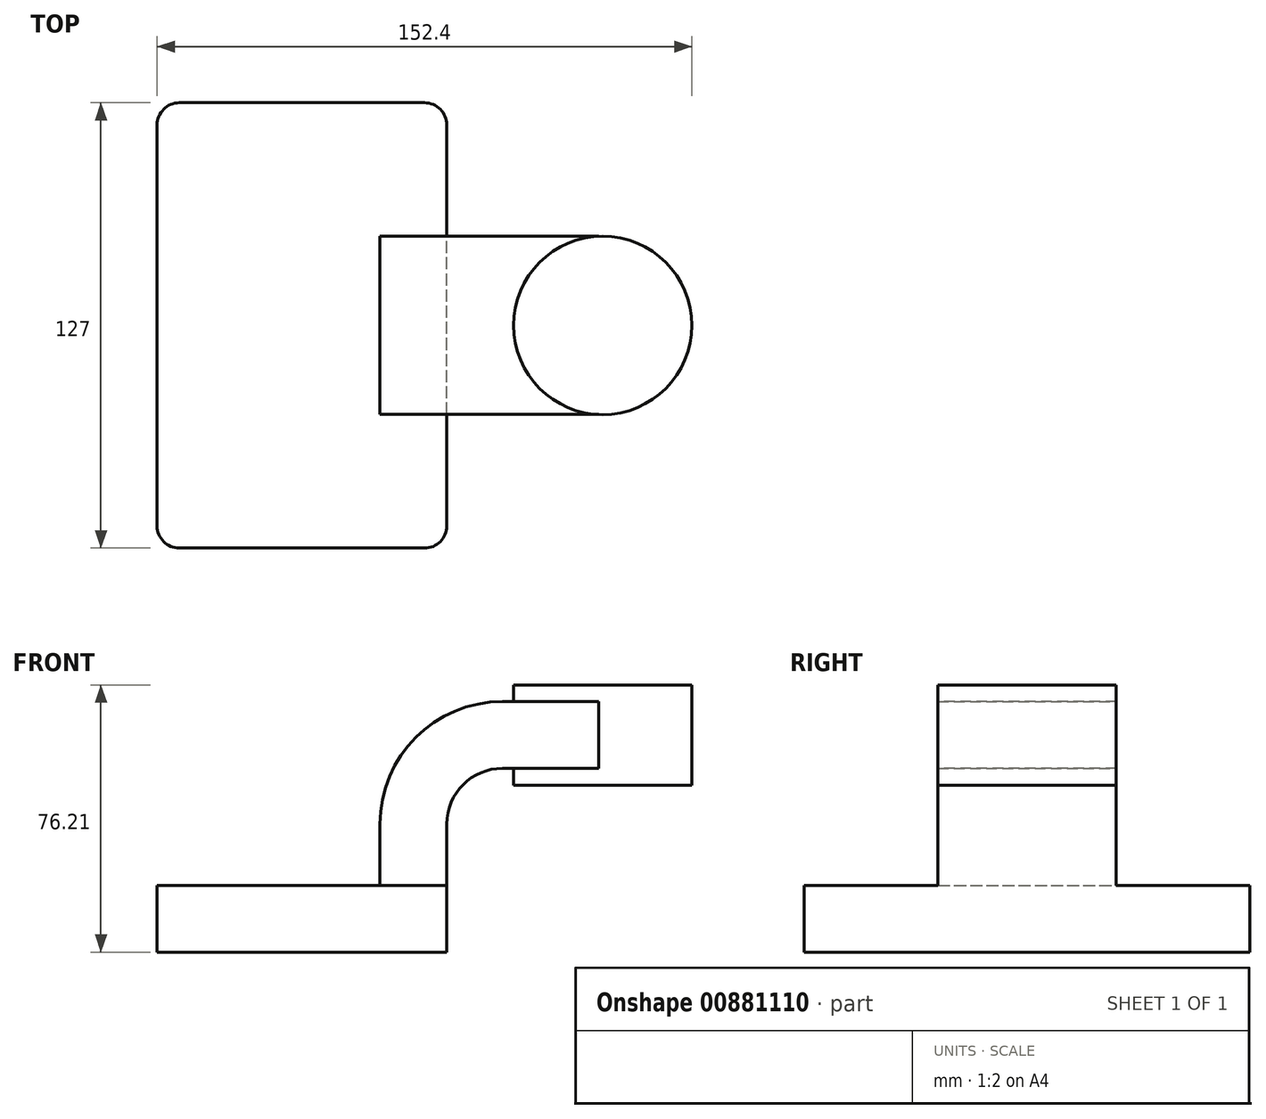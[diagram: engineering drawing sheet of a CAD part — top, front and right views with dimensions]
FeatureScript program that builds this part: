
annotation { "Feature Type Name" : "Feature", "Feature Type Description" : "" }
export const myFeature = defineFeature(function(context is Context, id is Id, definition is map)
    precondition{}
    {
        {
            var Q0;
            Q0=qCreatedBy(makeId("Front.planeOp"),FACE);
            var sketch = newSketch(context, id + "F0", { "sketchPlane" : qUnion([Q0])});
            skLineSegment(sketch, "E0.bottom", {"start": v(-41.27, -9.53) * mm, "end": v(41.28, -9.53) * mm});
            skLineSegment(sketch, "E0.top", {"start": v(-41.28, 9.53) * mm, "end": v(41.28, 9.53) * mm});
            skLineSegment(sketch, "E0.left", {"start": v(-41.28, -9.53) * mm, "end": v(-41.28, 9.53) * mm});
            skLineSegment(sketch, "E0.right", {"start": v(41.28, -9.53) * mm, "end": v(41.28, 9.52) * mm});
            skPoint(sketch, "E0.middle", {"position": v(0, 0) * mm});
            skLineSegment(sketch, "E1.bottom", {"start": v(60.33, 38.1) * mm, "end": v(111.12, 38.1) * mm});
            skLineSegment(sketch, "E1.top", {"start": v(60.33, 66.67) * mm, "end": v(111.12, 66.67) * mm});
            skLineSegment(sketch, "E1.left", {"start": v(60.33, 38.1) * mm, "end": v(60.33, 66.67) * mm});
            skLineSegment(sketch, "E1.right", {"start": v(111.12, 38.1) * mm, "end": v(111.12, 66.67) * mm});
            skPoint(sketch, "E1.middle", {"position": v(85.72, 52.39) * mm});
            skLineSegment(sketch, "E2", {"start": v(41.28, 9.52) * mm, "end": v(41.28, 27) * mm});
            skArc(sketch, "E3", {"start": v(41.27, 27) * mm, "mid": v(45.92, 38.23) * mm, "end": v(57.15, 42.88) * mm});
            skLineSegment(sketch, "E4", {"start": v(57.15, 42.88) * mm, "end": v(85.7, 42.88) * mm});
            skLineSegment(sketch, "E5.0", {"start": v(57.15, 61.93) * mm, "end": v(85.7, 61.93) * mm});
            skArc(sketch, "E5.1", {"start": v(22.22, 27) * mm, "mid": v(32.45, 51.7) * mm, "end": v(57.15, 61.93) * mm});
            skLineSegment(sketch, "E5.2", {"start": v(22.22, 9.52) * mm, "end": v(22.22, 27) * mm});
            skLineSegment(sketch, "E6", {"start": v(85.7, 66.67) * mm, "end": v(85.7, 38.1) * mm});
            skFitSpline(sketch, "E7", {"points": [v(-41.28, 9.53) * mm, v(57.15, 61.93) * mm], "startDerivative": vector(-0.14, 90.76) * mm, "endDerivative": vector(106.3, -1.28) * mm});
            skSolve(sketch);
        }
        {
            var Q0;
            Q0=makeQuery(id+"F0.imprint","IMPRINT",FACE,{"disambiguationData":[TD([[makeQuery(id+"F0.imprint","IMPRINT",EDGE,{"derivedFrom":sQuery(id+"F0.wireOp",EDGE,"E0.bottom")}),1.0]])]});
            extrude(context, id + "F1", {"entities" : qUnion([Q0]), "endBound" : BoundingType.SYMMETRIC, "depth" : 127 * mm, "offsetDistance" : 25.4 * mm});
        }
        {
            var Q0;
            Q0=makeQuery(id+"F0.imprint","IMPRINT",FACE,{"disambiguationData":[TD([[makeQuery(id+"F0.imprint","IMPRINT",EDGE,{"derivedFrom":sQuery(id+"F0.wireOp",EDGE,"E5.1")}),1.0]])]});
            extrude(context, id + "F2", {"entities" : qUnion([Q0]), "operationType" : NewBodyOperationType.ADD, "endBound" : BoundingType.SYMMETRIC, "depth" : 15.88 * mm, "offsetDistance" : 25.4 * mm});
        }
        {
            var Q0;
            {var subQ0=sQuery(id+"F0.wireOp",EDGE,"E4");var subQ1=sQuery(id+"F0.wireOp",EDGE,"E1.left");var subQ2=makeQuery(id+"F0.imprint","INTERSECT",VERTEX,{"derivedFrom":[subQ1,subQ0]});Q0=makeQuery(id+"F0.imprint","IMPRINT",FACE,{"disambiguationData":[TD([[makeQuery(id+"F0.imprint","IMPRINT",EDGE,{"disambiguationData":[TD([[subQ2,-1.0]])],"derivedFrom":subQ1}),-1.0]])]});}
            var Q1;
            {var subQ1=sQuery(id+"F0.wireOp",EDGE,"E2");Q1=makeQuery(id+"F0.imprint","IMPRINT",FACE,{"disambiguationData":[TD([[makeQuery(id+"F0.imprint","IMPRINT",EDGE,{"derivedFrom":subQ1}),1.0]])]});}
            extrude(context, id + "F3", {"entities" : qUnion([Q0, Q1]), "operationType" : NewBodyOperationType.ADD, "endBound" : BoundingType.SYMMETRIC, "depth" : 50.8 * mm, "offsetDistance" : 25.4 * mm});
        }
        {
            var Q0;
            {var subQ0=sQuery(id+"F0.wireOp",EDGE,"E1.right");Q0=makeQuery(id+"F0.imprint","IMPRINT",FACE,{"disambiguationData":[TD([[makeQuery(id+"F0.imprint","IMPRINT",EDGE,{"derivedFrom":subQ0}),1.0]])]});}
            var Q1;
            Q1=sQuery(id+"F0.wireOp",EDGE,"E6");
            revolve(context, id + "F4", {"operationType" : NewBodyOperationType.ADD, "surfaceOperationType" : NewSurfaceOperationType.NEW, "entities" : qUnion([Q0]), "axis" : qUnion([Q1]), "revolveType" : RevolveType.FULL});
        }
        {
            var Q0;
            Q0=makeQuery(id+"F1.opExtrude","CAP_EDGE",EDGE,{"disambiguationData":[OSD([sQuery(id+"F0.wireOp",EDGE,"E0.right")])],"isStart":false});
            var Q1;
            Q1=makeQuery(id+"F1.opExtrude","CAP_EDGE",EDGE,{"disambiguationData":[OSD([sQuery(id+"F0.wireOp",EDGE,"E0.left")])],"isStart":false});
            var Q2;
            Q2=makeQuery(id+"F1.opExtrude","CAP_EDGE",EDGE,{"disambiguationData":[OSD([sQuery(id+"F0.wireOp",EDGE,"E0.right")])],"isStart":true});
            var Q3;
            Q3=makeQuery(id+"F1.opExtrude","CAP_EDGE",EDGE,{"disambiguationData":[OSD([sQuery(id+"F0.wireOp",EDGE,"E0.left")])],"isStart":true});
            fillet(context, id + "F5", {"entities" : qUnion([Q0, Q1, Q2, Q3]), "radius" : 6.35 * mm, "tangentPropagation" : true, "allowEdgeOverflow" : false});
        }
    });
